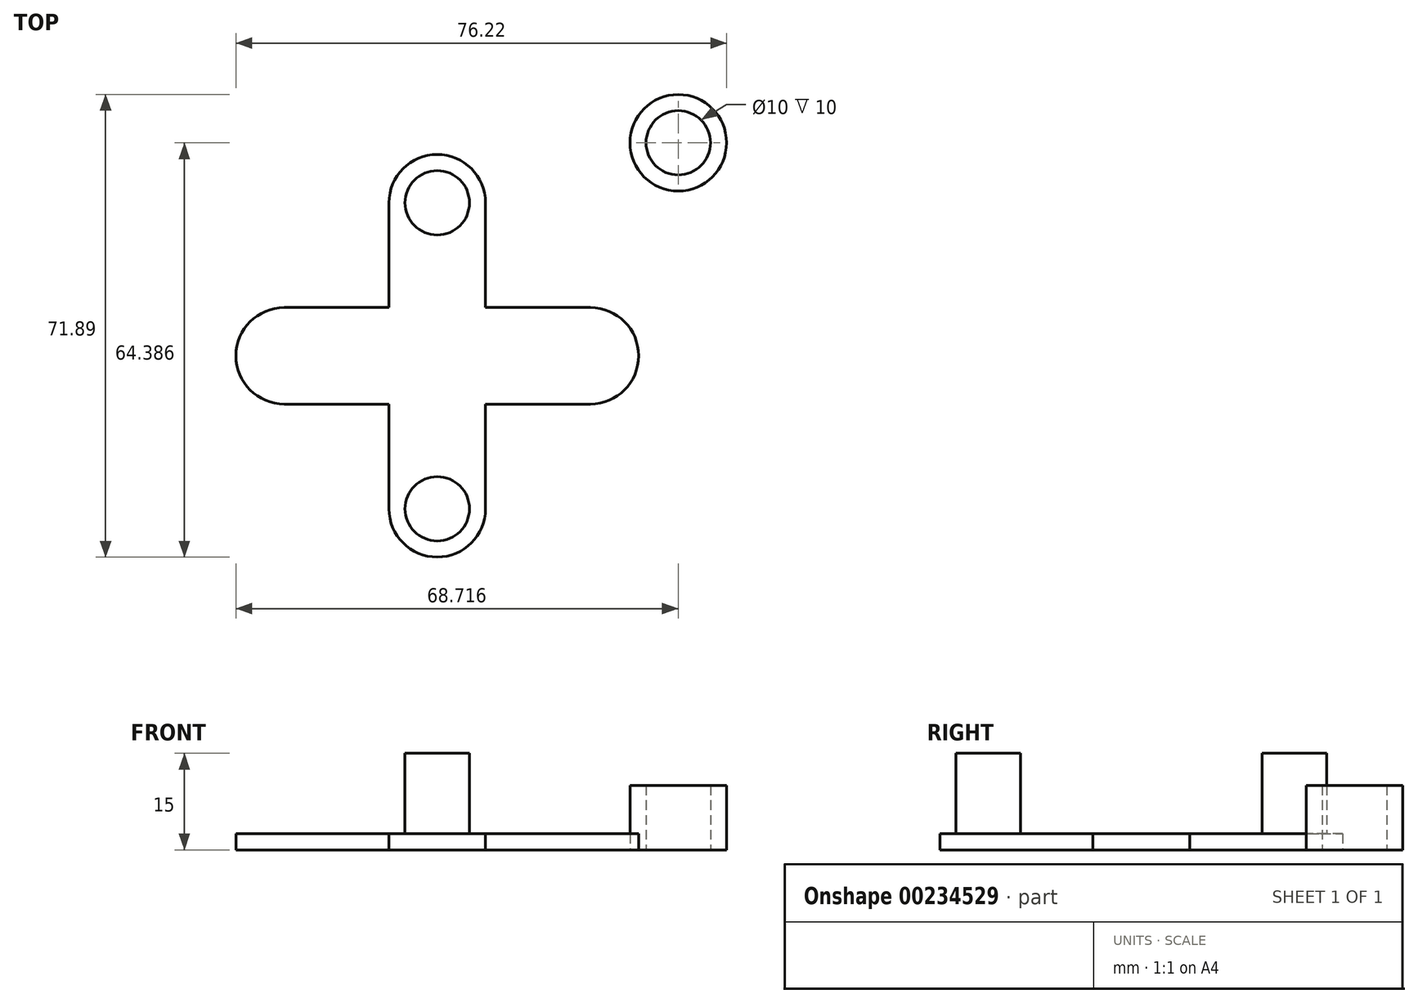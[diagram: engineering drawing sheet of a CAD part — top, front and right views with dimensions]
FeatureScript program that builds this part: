
annotation { "Feature Type Name" : "Feature", "Feature Type Description" : "" }
export const myFeature = defineFeature(function(context is Context, id is Id, definition is map)
    precondition{}
    {
        {
            var Q0;
            Q0=qCreatedBy(makeId("Top.planeOp"),FACE);
            var sketch = newSketch(context, id + "F0", { "sketchPlane" : qUnion([Q0])});
            skLineSegment(sketch, "E0", {"start": v(0, 23.78) * mm, "end": v(0, -23.78) * mm});
            skCircle(sketch, "E1", {"center": v(0, 23.78) * mm, "radius": 7.5 * mm});
            skCircle(sketch, "E2", {"center": v(0, -23.78) * mm, "radius": 7.5 * mm});
            skLineSegment(sketch, "E3", {"start": v(7.5, 23.78) * mm, "end": v(7.5, -23.78) * mm});
            skLineSegment(sketch, "E4", {"start": v(-7.5, -23.78) * mm, "end": v(-7.5, 23.78) * mm});
            skLineSegment(sketch, "E5", {"start": v(0, -23.78) * mm, "end": v(7.73, 0) * mm});
            skLineSegment(sketch, "E6", {"start": v(7.73, 0) * mm, "end": v(0, 23.78) * mm});
            skLineSegment(sketch, "E7.1.0", {"start": v(-23.78, 7.5) * mm, "end": v(23.78, 7.5) * mm});
            skLineSegment(sketch, "E7.1.1", {"start": v(23.78, -7.5) * mm, "end": v(-23.78, -7.5) * mm});
            skCircle(sketch, "E7.1.2", {"center": v(23.78, 0) * mm, "radius": 7.5 * mm});
            skCircle(sketch, "E7.1.3", {"center": v(-23.78, 0) * mm, "radius": 7.5 * mm});
            skPoint(sketch, "E7.center", {"position": v(0, 0) * mm});
            skLineSegment(sketch, "E7.anchor1", {"start": v(0, 0) * mm, "end": v(-7.5, -23.78) * mm, "construction": true});
            skLineSegment(sketch, "E7.anchor2", {"start": v(0, 0) * mm, "end": v(7.5, 23.78) * mm, "construction": true});
            skSolve(sketch);
        }
        {
            var Q0;
            {var subQ5=sQuery(id+"F0.wireOp",EDGE,"E4");Q0=makeQuery(id+"F0.imprint","IMPRINT",FACE,{"disambiguationData":[TD([[makeQuery(id+"F0.imprint","IMPRINT",EDGE,{"derivedFrom":subQ5}),-1.0]])]});}
            var Q1;
            {var subQ4=sQuery(id+"F0.wireOp",EDGE,"fzPgiqt2-BGiQ-etvl-xmxu-UWmpH7j9fk7d");var subQ5=sQuery(id+"F0.wireOp",EDGE,"E0");var subQ6=makeQuery(id+"F0.imprint","INTERSECT",VERTEX,{"derivedFrom":[subQ5,subQ4]});Q1=makeQuery(id+"F0.imprint","IMPRINT",FACE,{"disambiguationData":[TD([[makeQuery(id+"F0.imprint","IMPRINT",EDGE,{"disambiguationData":[TD([[subQ6,-1.0]])],"derivedFrom":subQ5}),-1.0]])]});}
            var Q2;
            {var subQ5=sQuery(id+"F0.wireOp",EDGE,"E1");var subQ6=sQuery(id+"F0.wireOp",EDGE,"E0");var subQ7=makeQuery(id+"F0.imprint","INTERSECT",VERTEX,{"derivedFrom":[subQ6,subQ5]});Q2=makeQuery(id+"F0.imprint","IMPRINT",FACE,{"disambiguationData":[TD([[makeQuery(id+"F0.imprint","IMPRINT",EDGE,{"disambiguationData":[TD([[subQ7,-1.0]])],"derivedFrom":subQ6}),1.0]])]});}
            var Q3;
            {var subQ0=sQuery(id+"F0.wireOp",EDGE,"E3");var subQ1=sQuery(id+"F0.wireOp",EDGE,"E2");var subQ2=makeQuery(id+"F0.imprint","INTERSECT",VERTEX,{"derivedFrom":[subQ1,subQ0]});Q3=makeQuery(id+"F0.imprint","IMPRINT",FACE,{"disambiguationData":[TD([[makeQuery(id+"F0.imprint","IMPRINT",EDGE,{"disambiguationData":[TD([[subQ2,-1.0]])],"derivedFrom":subQ1}),-1.0]])]});}
            var Q4;
            {var subQ0=sQuery(id+"F0.wireOp",EDGE,"E2");var subQ3=sQuery(id+"F0.wireOp",EDGE,"E0");var subQ4=makeQuery(id+"F0.imprint","INTERSECT",VERTEX,{"derivedFrom":[subQ3,subQ0]});Q4=makeQuery(id+"F0.imprint","IMPRINT",FACE,{"disambiguationData":[TD([[makeQuery(id+"F0.imprint","IMPRINT",EDGE,{"disambiguationData":[TD([[subQ4,-1.0]])],"derivedFrom":subQ3}),-1.0]])]});}
            var Q5;
            {var subQ0=sQuery(id+"F0.wireOp",EDGE,"E2");var subQ1=sQuery(id+"F0.wireOp",EDGE,"E0");var subQ2=makeQuery(id+"F0.imprint","INTERSECT",VERTEX,{"derivedFrom":[subQ1,subQ0]});Q5=makeQuery(id+"F0.imprint","IMPRINT",FACE,{"disambiguationData":[TD([[makeQuery(id+"F0.imprint","IMPRINT",EDGE,{"disambiguationData":[TD([[subQ2,-1.0]])],"derivedFrom":subQ1}),1.0]])]});}
            var Q6;
            {var subQ0=sQuery(id+"F0.wireOp",EDGE,"E3");var subQ1=sQuery(id+"F0.wireOp",EDGE,"E1");var subQ2=makeQuery(id+"F0.imprint","INTERSECT",VERTEX,{"derivedFrom":[subQ1,subQ0]});Q6=makeQuery(id+"F0.imprint","IMPRINT",FACE,{"disambiguationData":[TD([[makeQuery(id+"F0.imprint","IMPRINT",EDGE,{"disambiguationData":[TD([[subQ2,1.0]])],"derivedFrom":subQ1}),-1.0]])]});}
            var Q7;
            {var subQ0=sQuery(id+"F0.wireOp",EDGE,"fzPgiqt2-BGiQ-etvl-xmxu-UWmpH7j9fk7d");var subQ1=sQuery(id+"F0.wireOp",EDGE,"E0");var subQ2=makeQuery(id+"F0.imprint","INTERSECT",VERTEX,{"derivedFrom":[subQ1,subQ0]});Q7=makeQuery(id+"F0.imprint","IMPRINT",FACE,{"disambiguationData":[TD([[makeQuery(id+"F0.imprint","IMPRINT",EDGE,{"disambiguationData":[TD([[subQ2,-1.0]])],"derivedFrom":subQ1}),1.0]])]});}
            var Q8;
            {var subQ0=sQuery(id+"F0.wireOp",EDGE,"E6");var subQ1=sQuery(id+"F0.wireOp",EDGE,"E0");var subQ2=makeQuery(id+"F0.imprint","INTERSECT",VERTEX,{"derivedFrom":[subQ1,subQ0]});Q8=makeQuery(id+"F0.imprint","IMPRINT",FACE,{"disambiguationData":[TD([[makeQuery(id+"F0.imprint","IMPRINT",EDGE,{"disambiguationData":[TD([[subQ2,-1.0]])],"derivedFrom":subQ1}),-1.0]])]});}
            var Q9;
            {var subQ0=sQuery(id+"F0.wireOp",EDGE,"E5");var subQ1=sQuery(id+"F0.wireOp",EDGE,"E0");var subQ2=makeQuery(id+"F0.imprint","INTERSECT",VERTEX,{"derivedFrom":[subQ1,subQ0]});Q9=makeQuery(id+"F0.imprint","IMPRINT",FACE,{"disambiguationData":[TD([[makeQuery(id+"F0.imprint","IMPRINT",EDGE,{"disambiguationData":[TD([[subQ2,1.0]])],"derivedFrom":subQ1}),-1.0]])]});}
            var Q10;
            {var subQ0=sQuery(id+"F0.wireOp",EDGE,"E5");var subQ1=sQuery(id+"F0.wireOp",EDGE,"E0");var subQ2=makeQuery(id+"F0.imprint","INTERSECT",VERTEX,{"derivedFrom":[subQ1,subQ0]});Q10=makeQuery(id+"F0.imprint","IMPRINT",FACE,{"disambiguationData":[TD([[makeQuery(id+"F0.imprint","IMPRINT",EDGE,{"disambiguationData":[TD([[subQ2,1.0]])],"derivedFrom":subQ1}),1.0]])]});}
            var Q11;
            {var subQ0=sQuery(id+"F0.wireOp",EDGE,"E6");var subQ1=sQuery(id+"F0.wireOp",EDGE,"E0");var subQ2=makeQuery(id+"F0.imprint","INTERSECT",VERTEX,{"derivedFrom":[subQ1,subQ0]});Q11=makeQuery(id+"F0.imprint","IMPRINT",FACE,{"disambiguationData":[TD([[makeQuery(id+"F0.imprint","IMPRINT",EDGE,{"disambiguationData":[TD([[subQ2,-1.0]])],"derivedFrom":subQ1}),1.0]])]});}
            var Q12;
            {var subQ0=sQuery(id+"F0.wireOp",EDGE,"E7.1.1");var subQ1=sQuery(id+"F0.wireOp",EDGE,"E0");var subQ2=makeQuery(id+"F0.imprint","INTERSECT",VERTEX,{"derivedFrom":[subQ1,subQ0]});Q12=makeQuery(id+"F0.imprint","IMPRINT",FACE,{"disambiguationData":[TD([[makeQuery(id+"F0.imprint","IMPRINT",EDGE,{"disambiguationData":[TD([[subQ2,-1.0]])],"derivedFrom":subQ1}),1.0]])]});}
            var Q13;
            {var subQ0=sQuery(id+"F0.wireOp",EDGE,"E2");var subQ1=sQuery(id+"F0.wireOp",EDGE,"E5");var subQ2=makeQuery(id+"F0.imprint","INTERSECT",VERTEX,{"derivedFrom":[subQ1,subQ0]});Q13=makeQuery(id+"F0.imprint","IMPRINT",FACE,{"disambiguationData":[TD([[makeQuery(id+"F0.imprint","IMPRINT",EDGE,{"disambiguationData":[TD([[subQ2,-1.0]])],"derivedFrom":subQ1}),-1.0]])]});}
            var Q14;
            {var subQ0=sQuery(id+"F0.wireOp",EDGE,"E7.1.1");var subQ1=sQuery(id+"F0.wireOp",EDGE,"E5");var subQ2=makeQuery(id+"F0.imprint","INTERSECT",VERTEX,{"derivedFrom":[subQ1,subQ0]});Q14=makeQuery(id+"F0.imprint","IMPRINT",FACE,{"disambiguationData":[TD([[makeQuery(id+"F0.imprint","IMPRINT",EDGE,{"disambiguationData":[TD([[subQ2,-1.0]])],"derivedFrom":subQ1}),-1.0]])]});}
            var Q15;
            {var subQ0=sQuery(id+"F0.wireOp",EDGE,"E7.1.0");var subQ1=sQuery(id+"F0.wireOp",EDGE,"E6");var subQ2=makeQuery(id+"F0.imprint","INTERSECT",VERTEX,{"derivedFrom":[subQ1,subQ0]});Q15=makeQuery(id+"F0.imprint","IMPRINT",FACE,{"disambiguationData":[TD([[makeQuery(id+"F0.imprint","IMPRINT",EDGE,{"disambiguationData":[TD([[subQ2,-1.0]])],"derivedFrom":subQ1}),-1.0]])]});}
            var Q16;
            {var subQ0=sQuery(id+"F0.wireOp",EDGE,"E3");var subQ1=sQuery(id+"F0.wireOp",EDGE,"E6");var subQ2=makeQuery(id+"F0.imprint","INTERSECT",VERTEX,{"derivedFrom":[subQ1,subQ0]});Q16=makeQuery(id+"F0.imprint","IMPRINT",FACE,{"disambiguationData":[TD([[makeQuery(id+"F0.imprint","IMPRINT",EDGE,{"disambiguationData":[TD([[subQ2,-1.0]])],"derivedFrom":subQ1}),-1.0]])]});}
            var Q17;
            {var subQ8=sQuery(id+"F0.wireOp",EDGE,"E6");var subQ9=sQuery(id+"F0.wireOp",EDGE,"E5");var subQ10=makeQuery(id+"F0.imprint","INTERSECT",VERTEX,{"derivedFrom":[subQ9,subQ8]});Q17=makeQuery(id+"F0.imprint","IMPRINT",FACE,{"disambiguationData":[TD([[makeQuery(id+"F0.imprint","IMPRINT",EDGE,{"disambiguationData":[TD([[subQ10,1.0]])],"derivedFrom":subQ9}),-1.0]])]});}
            var Q18;
            {var subQ0=sQuery(id+"F0.wireOp",EDGE,"E1");var subQ1=sQuery(id+"F0.wireOp",EDGE,"E0");var subQ2=makeQuery(id+"F0.imprint","INTERSECT",VERTEX,{"derivedFrom":[subQ1,subQ0]});Q18=makeQuery(id+"F0.imprint","IMPRINT",FACE,{"disambiguationData":[TD([[makeQuery(id+"F0.imprint","IMPRINT",EDGE,{"disambiguationData":[TD([[subQ2,-1.0]])],"derivedFrom":subQ1}),1.0]])]});}
            var Q19;
            {var subQ0=sQuery(id+"F0.wireOp",EDGE,"E7.1.0");var subQ1=sQuery(id+"F0.wireOp",EDGE,"E0");var subQ2=makeQuery(id+"F0.imprint","INTERSECT",VERTEX,{"derivedFrom":[subQ1,subQ0]});Q19=makeQuery(id+"F0.imprint","IMPRINT",FACE,{"disambiguationData":[TD([[makeQuery(id+"F0.imprint","IMPRINT",EDGE,{"disambiguationData":[TD([[subQ2,-1.0]])],"derivedFrom":subQ1}),1.0]])]});}
            var Q20;
            {var subQ0=sQuery(id+"F0.wireOp",EDGE,"E6");var subQ1=sQuery(id+"F0.wireOp",EDGE,"E5");var subQ2=makeQuery(id+"F0.imprint","INTERSECT",VERTEX,{"derivedFrom":[subQ1,subQ0]});Q20=makeQuery(id+"F0.imprint","IMPRINT",FACE,{"disambiguationData":[TD([[makeQuery(id+"F0.imprint","IMPRINT",EDGE,{"disambiguationData":[TD([[subQ2,1.0]])],"derivedFrom":subQ1}),1.0]])]});}
            var Q21;
            {var subQ0=sQuery(id+"F0.wireOp",EDGE,"E7.1.2");var subQ1=makeQuery(id+"F0.imprint","INTERSECT",VERTEX,{"derivedFrom":[sQuery(id+"F0.wireOp",EDGE,"E7.1.0"),subQ0]});Q21=makeQuery(id+"F0.imprint","IMPRINT",FACE,{"disambiguationData":[TD([[makeQuery(id+"F0.imprint","IMPRINT",EDGE,{"disambiguationData":[TD([[subQ1,1.0]])],"derivedFrom":subQ0}),1.0]])]});}
            var Q22;
            {var subQ0=sQuery(id+"F0.wireOp",EDGE,"E7.1.3");var subQ1=sQuery(id+"F0.wireOp",EDGE,"E7.1.0");var subQ2=makeQuery(id+"F0.imprint","INTERSECT",VERTEX,{"derivedFrom":[subQ1,subQ0]});Q22=makeQuery(id+"F0.imprint","IMPRINT",FACE,{"disambiguationData":[TD([[makeQuery(id+"F0.imprint","IMPRINT",EDGE,{"disambiguationData":[TD([[subQ2,-1.0]])],"derivedFrom":subQ1}),-1.0]])]});}
            var Q23;
            {var subQ0=sQuery(id+"F0.wireOp",EDGE,"E7.1.3");var subQ1=makeQuery(id+"F0.imprint","INTERSECT",VERTEX,{"derivedFrom":[sQuery(id+"F0.wireOp",EDGE,"E7.1.0"),subQ0]});Q23=makeQuery(id+"F0.imprint","IMPRINT",FACE,{"disambiguationData":[TD([[makeQuery(id+"F0.imprint","IMPRINT",EDGE,{"disambiguationData":[TD([[subQ1,1.0]])],"derivedFrom":subQ0}),1.0]])]});}
            extrude(context, id + "F1", {"entities" : qUnion([Q0, Q1, Q2, Q3, Q4, Q5, Q6, Q7, Q8, Q9, Q10, Q11, Q12, Q13, Q14, Q15, Q16, Q17, Q18, Q19, Q20, Q21, Q22, Q23]), "depth" : 2.5 * mm});
        }
        {
            var Q0;
            Q0=makeQuery(id+"F1.opExtrude","CAP_FACE",FACE,{"disambiguationData":[OSD([sQuery(id+"F0.wireOp",EDGE,"E7.1.0"),sQuery(id+"F0.wireOp",EDGE,"E7.1.1"),sQuery(id+"F0.wireOp",EDGE,"E7.1.2"),sQuery(id+"F0.wireOp",EDGE,"E7.1.3"),sQuery(id+"F0.wireOp",EDGE,"E3"),sQuery(id+"F0.wireOp",EDGE,"E4"),sQuery(id+"F0.wireOp",EDGE,"E2"),sQuery(id+"F0.wireOp",EDGE,"E1")])],"isStart":false});
            var sketch = newSketch(context, id + "F2", { "sketchPlane" : qUnion([Q0])});
            skCircle(sketch, "E8", {"center": v(0, 23.78) * mm, "radius": 5 * mm});
            skCircle(sketch, "E9", {"center": v(0, -23.78) * mm, "radius": 5 * mm});
            skSolve(sketch);
        }
        {
            var Q0;
            Q0 = qSketchRegion(id + "F2", true);
            extrude(context, id + "F3", {"entities" : qUnion([Q0]), "operationType" : NewBodyOperationType.ADD, "depth" : 12.5 * mm});
        }
        {
            var Q0;
            Q0=qCreatedBy(makeId("Top.planeOp"),FACE);
            var sketch = newSketch(context, id + "F4", { "sketchPlane" : qUnion([Q0])});
            skCircle(sketch, "E10", {"center": v(37.44, 33.1) * mm, "radius": 7.5 * mm});
            skCircle(sketch, "E11", {"center": v(37.44, 33.1) * mm, "radius": 5 * mm});
            skSolve(sketch);
        }
        {
            var Q0;
            Q0=makeQuery(id+"F4.imprint","IMPRINT",FACE,{"disambiguationData":[TD([[makeQuery(id+"F4.imprint","IMPRINT",EDGE,{"derivedFrom":sQuery(id+"F4.wireOp",EDGE,"E10")}),1.0]])]});
            extrude(context, id + "F5", {"entities" : qUnion([Q0]), "depth" : 10 * mm});
        }
    });
